# Revit family: REVIT-MXS-2017
name_source: partatom
category: Mechanical Equipment
revit_build: Autodesk Revit 2017 (Build: 20190507_1515(x64)
units: mm (PartAtom-declared; Revit-internal decimal feet)

## family parameters
Always vertical = Yes
Cut with Voids When Loaded = No
Part Type = Normal
Room Calculation Point = No
Round Connector Dimension = Use Radius
Shared = No
Work Plane-Based = No

## types (6) — shared parameters
A = 9"
Air Inlet Radius = 1 1/2"
Assembly Code = D3040400
B = 6 1/4"
Burner Depth = 10 1/4"
Burner Height = 14"
Burner Width = 15 1/4"
Cold Water NPT = 2"
Cold Water Radius = 1"
Current = 2 A
Description = Maxim Series Gas Water Heater
Disclaimer = This rendering is for building modeling purposes only. Submittal/catalog is still the contract document. PVI reserves the right to change design and specification without notice.
Drain NPT = 1"
Drain Radius = 1/2"
Energy Radius = 4"
Gas Inlet NPT = 3/4"
Gas Inlet Radius = 3/8"
Gas Inlet Y = 4 1/2"
Gas Inlet Z = 8 3/4"
Height to Cold Inlet = 25"
Height to Drain = 18"
Height to Energy = 7"
Height to Hot Outlet = 62"
Height to Relief = 62 5/8"
Hot Water NPT = 2"
Hot Water Radius = 1"
Manufacturer = PVI Industries, LLC
Maximum Static Gas Pressure = 10.50 in-wg
Minimum Gas Pressure = 4.50 in-wg
RandD Angle = 45.00°
Relief Valve NPT = 3/4"
Relief Valve Radius = 3/8"
URL = www.pvi.com
Unit Height = 72"
Voltage = 120 V

## per-type parameters (varying)
| type | Cold Water Extension | Control Panel Extension | Drain Extension | Energy Extension | Flue Diameter | Flue Radius | Hot Water Extension | Input | Rear Skid Extension | Recovery Rate 40F to 140F | Recovery Rate 70F to 140F | Relief Extension | Skid Center Dist | Skid Length | Skid Spacing | Unit Radius | Weight |
| 40 L 250A-MXS | 23 1/2" | 29 1/2" | 26 3/8" | 25" | 7" | 3 1/2" | 23 1/2" | 399000 Btu/h | 22 1/2" | 500 gph | 400 gph | 23 1/2" | 12 1/4" | 45" | 24 1/2" | 22 1/2" | 1520 |
| 27 L 250A-MXS | 23 1/2" | 29 1/2" | 26 3/8" | 25" | 6" | 3" | 23 1/2" | 270000 Btu/h | 22 1/2" | 270 gph | 340 gph | 23 1/2" | 12 1/4" | 45" | 24 1/2" | 22 1/2" | 1470 |
| 40 L 125A-MXS | 18 1/8" | 24 1/8" | 21" | 19 5/8" | 7" | 3 1/2" | 18 1/8" | 399000 Btu/h | 17 1/8" | 390 gph | 490 gph | 18 1/8" | 10 1/4" | 34 1/2" | 20 1/2" | 17 1/8" | 1130 |
| 27 L 125A-MXS | 18 1/8" | 24 1/8" | 21" | 19 5/8" | 6" | 3" | 18 1/8" | 270000 Btu/h | 17 1/8" | 260 gph | 330 gph | 18 1/8" | 10 1/4" | 34 1/2" | 20 1/2" | 17 1/8" | 1070 |
| 20 L 125A-MXS | 18 1/8" | 24 1/8" | 21" | 19 5/8" | 5" | 2 1/2" | 18 1/8" | 199000 Btu/h | 17 1/8" | 195 gph | 245 gph | 18 1/8" | 10 1/4" | 34 1/2" | 20 1/2" | 17 1/8" | 1020 |
| 20 L 119A-MXS | 18 1/8" | 24 1/8" | 21" | 19 5/8" | 5" | 2 1/2" | 18 1/8" | 199000 Btu/h | 17 1/8" | 198 gph | 276 gph | 18 1/8" | 10 1/4" | 34 1/2" | 20 1/2" | 17 1/8" | 980 |

note: column(s) folded — value = type name in every type: Model

## geometry (parser evidence)
native form markers: Blend x2, Sweep x3
no freeform markers — native parametric forms only
